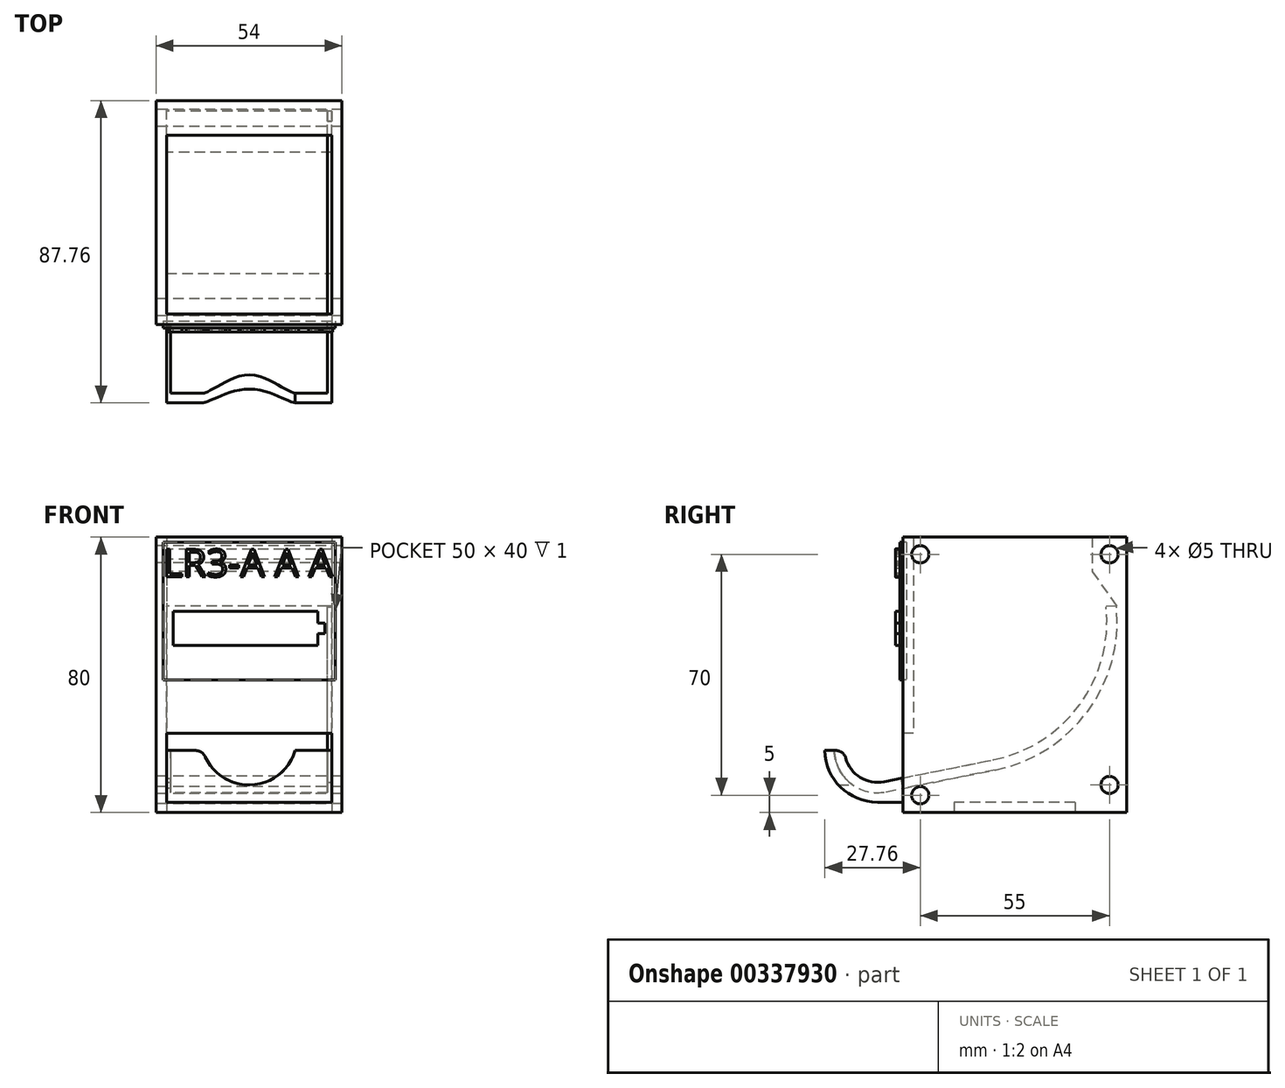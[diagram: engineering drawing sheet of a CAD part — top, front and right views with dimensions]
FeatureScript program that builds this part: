
annotation { "Feature Type Name" : "Feature", "Feature Type Description" : "" }
export const myFeature = defineFeature(function(context is Context, id is Id, definition is map)
    precondition{}
    {
        {
            var Q0;
            Q0=qCreatedBy(makeId("Top.planeOp"),FACE);
            var sketch = newSketch(context, id + "F0", { "sketchPlane" : qUnion([Q0])});
            skLineSegment(sketch, "E0", {"start": v(-27, 65) * mm, "end": v(-27, 0) * mm});
            skLineSegment(sketch, "E1", {"start": v(-27, 0) * mm, "end": v(27, 0) * mm});
            skLineSegment(sketch, "E2", {"start": v(27, 0) * mm, "end": v(27, 65) * mm});
            skLineSegment(sketch, "E3.0", {"start": v(-24, 65) * mm, "end": v(-24, 3) * mm});
            skLineSegment(sketch, "E4.0", {"start": v(-24, 3) * mm, "end": v(24, 3) * mm});
            skLineSegment(sketch, "E5.0", {"start": v(24, 3) * mm, "end": v(24, 65) * mm});
            skLineSegment(sketch, "E6", {"start": v(-27, 65) * mm, "end": v(-24, 65) * mm});
            skLineSegment(sketch, "E7", {"start": v(24, 65) * mm, "end": v(27, 65) * mm});
            skSolve(sketch);
        }
        {
            var Q0;
            Q0=qSketchRegion(id+"F0",true);
            extrude(context, id + "F1", {"entities" : qUnion([Q0]), "depth" : 80 * mm});
        }
        {
            var Q0;
            Q0=makeQuery(id+"F1.opExtrude","SWEPT_FACE",FACE,{"disambiguationData":[OSD([sQuery(id+"F0.wireOp",EDGE,"E1")])]});
            var sketch = newSketch(context, id + "F2", { "sketchPlane" : qUnion([Q0])});
            skLineSegment(sketch, "E8.bottom", {"start": v(-24, 3) * mm, "end": v(24, 3) * mm});
            skLineSegment(sketch, "E8.top", {"start": v(-24, 23) * mm, "end": v(24, 23) * mm});
            skLineSegment(sketch, "E8.left", {"start": v(-24, 3) * mm, "end": v(-24, 23) * mm});
            skLineSegment(sketch, "E8.right", {"start": v(24, 3) * mm, "end": v(24, 23) * mm});
            skSolve(sketch);
        }
        {
            var Q0;
            Q0=makeQuery(id+"F2.imprint","IMPRINT",FACE,{"disambiguationData":[TD([[makeQuery(id+"F2.imprint","IMPRINT",EDGE,{"derivedFrom":sQuery(id+"F2.wireOp",EDGE,"E8.bottom")}),1.0]])]});
            extrude(context, id + "F3", {"entities" : qUnion([Q0]), "operationType" : NewBodyOperationType.REMOVE, "endBound" : BoundingType.THROUGH_ALL, "oppositeDirection" : true, "depth" : 25 * mm});
        }
        {
            var Q0;
            {var subQ1=sQuery(id+"F0.wireOp",EDGE,"E4.0");Q0=makeQuery(id+"F3.boolean.opBoolean","SPLIT",FACE,{"disambiguationData":[TD([makeQuery(id+"F3.opExtrude","SWEPT_FACE",FACE,{"disambiguationData":[OSD([sQuery(id+"F2.wireOp",EDGE,"E8.bottom")])]})])],"derivedFrom":makeQuery(id+"F1.opExtrude","SWEPT_FACE",FACE,{"disambiguationData":[OSD([subQ1])]})});}
            extrude(context, id + "F4", {"entities" : qUnion([Q0]), "operationType" : NewBodyOperationType.ADD, "depth" : 11.8 * mm});
        }
        {
            var Q0;
            Q0=makeQuery(id+"F1.opExtrude","SWEPT_FACE",FACE,{"disambiguationData":[OSD([sQuery(id+"F0.wireOp",EDGE,"E1")])]});
            var sketch = newSketch(context, id + "F5", { "sketchPlane" : qUnion([Q0])});
            skLineSegment(sketch, "E9.bottom", {"start": v(-25, 78.5) * mm, "end": v(25, 78.5) * mm});
            skLineSegment(sketch, "E9.top", {"start": v(-25, 38.5) * mm, "end": v(25, 38.5) * mm});
            skLineSegment(sketch, "E9.left", {"start": v(-25, 78.5) * mm, "end": v(-25, 38.5) * mm});
            skLineSegment(sketch, "E9.right", {"start": v(25, 78.5) * mm, "end": v(25, 38.5) * mm});
            skSolve(sketch);
        }
        {
            var Q0;
            Q0=qSketchRegion(id+"F5",true);
            extrude(context, id + "F6", {"entities" : qUnion([Q0]), "operationType" : NewBodyOperationType.REMOVE, "oppositeDirection" : true, "depth" : 1 * mm});
        }
        {
            var Q0;
            Q0=qSketchRegion(id+"F5",true);
            extrude(context, id + "F7", {"entities" : qUnion([Q0]), "depth" : 1 * mm});
        }
        {
            var Q0;
            Q0=makeQuery(id+"F7.opExtrude","CAP_FACE",FACE,{"disambiguationData":[OSD([sQuery(id+"F5.wireOp",EDGE,"E9.bottom"),sQuery(id+"F5.wireOp",EDGE,"E9.top"),sQuery(id+"F5.wireOp",EDGE,"E9.left"),sQuery(id+"F5.wireOp",EDGE,"E9.right")])],"isStart":false});
            var sketch = newSketch(context, id + "F8", { "sketchPlane" : qUnion([Q0])});
            skText(sketch, "E10", { "text": "LR3-A A A", "fontName": "OpenSans-Regular.ttf"});
            const initialGuessF8  = {"E10": [-0.02508, 0.0685, 1, 0, 0.008]};
            skSetInitialGuess(sketch, initialGuessF8);
            skSolve(sketch);
        }
        {
            var Q0;
            Q0=makeQuery(id+"F8.imprint","IMPRINT",FACE,{"disambiguationData":[TD([[makeQuery(id+"F8.imprint","IMPRINT",EDGE,{"derivedFrom":sQuery(id+"F8.wireOp",EDGE,"E10.sketch_text.stroke-0")}),1.0]])]});
            var sketch = newSketch(context, id + "F9", { "sketchPlane" : qUnion([Q0])});
            skLineSegment(sketch, "E11.bottom", {"start": v(-22, 58.5) * mm, "end": v(20, 58.5) * mm});
            skLineSegment(sketch, "E11.top", {"start": v(-22, 48.5) * mm, "end": v(20, 48.5) * mm});
            skLineSegment(sketch, "E11.left", {"start": v(-22, 58.5) * mm, "end": v(-22, 48.5) * mm});
            skLineSegment(sketch, "E11.right", {"start": v(20, 58.5) * mm, "end": v(20, 55) * mm});
            skPoint(sketch, "E12.oppositeSnap0", {"position": v(20, 53.5) * mm});
            skLineSegment(sketch, "E12.bottom", {"start": v(20, 55) * mm, "end": v(22, 55) * mm});
            skLineSegment(sketch, "E13.trimOffspring", {"start": v(20, 52) * mm, "end": v(20, 48.5) * mm});
            skLineSegment(sketch, "E14", {"start": v(22, 55) * mm, "end": v(22, 52) * mm});
            skLineSegment(sketch, "E15", {"start": v(22, 52) * mm, "end": v(20, 52) * mm});
            skSolve(sketch);
        }
        {
            var Q0;
            Q0=makeQuery(id+"F9.imprint","IMPRINT",FACE,{"disambiguationData":[TD([[makeQuery(id+"F9.imprint","IMPRINT",EDGE,{"derivedFrom":sQuery(id+"F9.wireOp",EDGE,"E11.bottom")}),-1.0]])]});
            extrude(context, id + "F10", {"entities" : qUnion([Q0]), "operationType" : NewBodyOperationType.ADD, "depth" : 1.2 * mm});
        }
        {
            var Q0;
            Q0=qSketchRegion(id+"F8",true);
            extrude(context, id + "F11", {"entities" : qUnion([Q0]), "operationType" : NewBodyOperationType.ADD, "depth" : 1.2 * mm});
        }
        {
            var Q0;
            Q0=makeQuery(id+"F1.opExtrude","SWEPT_FACE",FACE,{"disambiguationData":[OSD([sQuery(id+"F0.wireOp",EDGE,"E7")])]});
            var sketch = newSketch(context, id + "F12", { "sketchPlane" : qUnion([Q0])});
            skLineSegment(sketch, "E16.bottom", {"start": v(-24, 3) * mm, "end": v(24, 3) * mm});
            skLineSegment(sketch, "E16.top", {"start": v(-24, 0) * mm, "end": v(24, 0) * mm});
            skLineSegment(sketch, "E16.left", {"start": v(-24, 3) * mm, "end": v(-24, 0) * mm});
            skLineSegment(sketch, "E16.right", {"start": v(24, 3) * mm, "end": v(24, 0) * mm});
            skSolve(sketch);
        }
        {
            var Q0;
            Q0=makeQuery(id+"F12.imprint","IMPRINT",FACE,{"disambiguationData":[TD([[makeQuery(id+"F12.imprint","IMPRINT",EDGE,{"derivedFrom":sQuery(id+"F12.wireOp",EDGE,"E16.bottom")}),-1.0]])]});
            extrude(context, id + "F13", {"entities" : qUnion([Q0]), "operationType" : NewBodyOperationType.ADD, "oppositeDirection" : true, "depth" : 15 * mm});
        }
        {
            var Q0;
            Q0=qCreatedBy(makeId("Right.planeOp"),FACE);
            var sketch = newSketch(context, id + "F14", { "sketchPlane" : qUnion([Q0])});
            skLineSegment(sketch, "E17", {"start": v(65, 80) * mm, "end": v(55, 80) * mm});
            skLineSegment(sketch, "E18", {"start": v(55, 80) * mm, "end": v(55, 70) * mm});
            skLineSegment(sketch, "E19", {"start": v(55, 70) * mm, "end": v(62, 60) * mm});
            skLineSegment(sketch, "E20", {"start": v(65, 80) * mm, "end": v(65, 3) * mm});
            skLineSegment(sketch, "E21", {"start": v(65, 3) * mm, "end": v(-7.46, 3) * mm});
            skArc(sketch, "E22", {"start": v(26.86, 12.37) * mm, "mid": v(53.63, 29.4) * mm, "end": v(62, 60) * mm});
            skLineSegment(sketch, "E23", {"start": v(-22.76, 18) * mm, "end": v(-20, 18) * mm});
            skLineSegment(sketch, "E24", {"start": v(26.86, 12.37) * mm, "end": v(-5, 6) * mm});
            skArc(sketch, "E25", {"start": v(-5, 6) * mm, "mid": v(-15.3, 8.5) * mm, "end": v(-20, 18) * mm});
            skArc(sketch, "E26", {"start": v(-7.46, 3) * mm, "mid": v(-18.17, 7.38) * mm, "end": v(-22.76, 18) * mm});
            skPoint(sketch, "E27", {"position": v(0, 7) * mm});
            skSolve(sketch);
        }
        {
            var Q0;
            Q0=makeQuery(id+"F14.imprint","IMPRINT",FACE,{"disambiguationData":[TD([[makeQuery(id+"F14.imprint","IMPRINT",EDGE,{"derivedFrom":sQuery(id+"F14.wireOp",EDGE,"E17")}),1.0]])]});
            extrude(context, id + "F15", {"entities" : qUnion([Q0]), "endBound" : BoundingType.SYMMETRIC, "depth" : 48 * mm});
        }
        {
            var Q0;
            Q0=qCreatedBy(makeId("Right.planeOp"),FACE);
            var sketch = newSketch(context, id + "F16", { "sketchPlane" : qUnion([Q0])});
            skCircle(sketch, "E28", {"center": v(60, 75) * mm, "radius": 2.5 * mm});
            skCircle(sketch, "E29", {"center": v(60, 8) * mm, "radius": 2.5 * mm});
            skCircle(sketch, "E30", {"center": v(5, 75) * mm, "radius": 2.5 * mm});
            skCircle(sketch, "E31", {"center": v(5, 5) * mm, "radius": 2.5 * mm});
            skSolve(sketch);
        }
        {
            var Q0;
            Q0=qSketchRegion(id+"F16",true);
            extrude(context, id + "F17", {"entities" : qUnion([Q0]), "operationType" : NewBodyOperationType.REMOVE, "endBound" : BoundingType.SYMMETRIC, "depth" : 60 * mm});
        }
        {
            var Q0;
            Q0=makeQuery(id+"F15.opExtrude","SWEPT_FACE",FACE,{"disambiguationData":[OSD([sQuery(id+"F14.wireOp",EDGE,"E23")])]});
            var sketch = newSketch(context, id + "F18", { "sketchPlane" : qUnion([Q0])});
            skLineSegment(sketch, "E32.bottom", {"start": v(22.8, -20) * mm, "end": v(24, -20) * mm});
            skLineSegment(sketch, "E32.top", {"start": v(22.8, -17) * mm, "end": v(24, -17) * mm});
            skLineSegment(sketch, "E32.left", {"start": v(22.8, -20) * mm, "end": v(22.8, -17) * mm});
            skLineSegment(sketch, "E32.right", {"start": v(24, -20) * mm, "end": v(24, -17) * mm});
            skLineSegment(sketch, "E33.bottom", {"start": v(-24, -20) * mm, "end": v(-22.8, -20) * mm});
            skLineSegment(sketch, "E33.top", {"start": v(-24, -17) * mm, "end": v(-22.8, -17) * mm});
            skLineSegment(sketch, "E33.left", {"start": v(-24, -20) * mm, "end": v(-24, -17) * mm});
            skLineSegment(sketch, "E33.right", {"start": v(-22.8, -20) * mm, "end": v(-22.8, -17) * mm});
            skSolve(sketch);
        }
        {
            var Q0;
            Q0=makeQuery(id+"F18.imprint","IMPRINT",FACE,{"disambiguationData":[TD([[makeQuery(id+"F18.imprint","IMPRINT",EDGE,{"derivedFrom":sQuery(id+"F18.wireOp",EDGE,"E32.bottom")}),-1.0]])]});
            var Q1;
            Q1=makeQuery(id+"F15.opExtrude","CAP_EDGE",EDGE,{"disambiguationData":[OSD([sQuery(id+"F14.wireOp",EDGE,"E25")])],"isStart":false});
            var Q2;
            Q2=makeQuery(id+"F15.opExtrude","CAP_EDGE",EDGE,{"disambiguationData":[OSD([sQuery(id+"F14.wireOp",EDGE,"E24")])],"isStart":false});
            var Q3;
            Q3=makeQuery(id+"F15.opExtrude","CAP_EDGE",EDGE,{"disambiguationData":[OSD([sQuery(id+"F14.wireOp",EDGE,"E22")])],"isStart":false});
            sweep(context, id + "F19", {"operationType" : NewBodyOperationType.ADD, "profiles" : qUnion([Q0]), "path" : qUnion([Q1, Q2, Q3])});
        }
        {
            var Q0;
            Q0=makeQuery(id+"F18.imprint","IMPRINT",FACE,{"disambiguationData":[TD([[makeQuery(id+"F18.imprint","IMPRINT",EDGE,{"derivedFrom":sQuery(id+"F18.wireOp",EDGE,"E33.bottom")}),-1.0]])]});
            var Q1;
            Q1=makeQuery(id+"F15.opExtrude","CAP_EDGE",EDGE,{"disambiguationData":[OSD([sQuery(id+"F14.wireOp",EDGE,"E25")])],"isStart":true});
            var Q2;
            Q2=makeQuery(id+"F15.opExtrude","CAP_EDGE",EDGE,{"disambiguationData":[OSD([sQuery(id+"F14.wireOp",EDGE,"E24")])],"isStart":true});
            var Q3;
            Q3=makeQuery(id+"F15.opExtrude","CAP_EDGE",EDGE,{"disambiguationData":[OSD([sQuery(id+"F14.wireOp",EDGE,"E22")])],"isStart":true});
            sweep(context, id + "F20", {"operationType" : NewBodyOperationType.ADD, "profiles" : qUnion([Q0]), "path" : qUnion([Q1, Q2, Q3])});
        }
        {
            var Q0;
            Q0=qCreatedBy(makeId("Front.planeOp"),FACE);
            var sketch = newSketch(context, id + "F21", { "sketchPlane" : qUnion([Q0])});
            skArc(sketch, "E34", {"start": v(-13.42, 18) * mm, "mid": v(0, 8) * mm, "end": v(13.42, 18) * mm});
            skLineSegment(sketch, "E35", {"start": v(-13.42, 18) * mm, "end": v(13.42, 18) * mm});
            skSolve(sketch);
        }
        {
            var Q0;
            Q0=makeQuery(id+"F21.imprint","IMPRINT",FACE,{"disambiguationData":[TD([[makeQuery(id+"F21.imprint","IMPRINT",EDGE,{"derivedFrom":sQuery(id+"F21.wireOp",EDGE,"E34")}),1.0]])]});
            extrude(context, id + "F22", {"entities" : qUnion([Q0]), "operationType" : NewBodyOperationType.REMOVE, "endBound" : BoundingType.THROUGH_ALL, "depth" : 25 * mm});
        }
        {
            var Q0;
            {var subQ0=sQuery(id+"F21.wireOp",EDGE,"E35");var subQ1=sQuery(id+"F21.wireOp",EDGE,"E34");Q0=makeQuery(id+"F22.boolean.opBoolean","COPY",EDGE,{"derivedFrom":makeQuery(id+"F22.opExtrude","SWEPT_EDGE",EDGE,{"disambiguationData":[OSD([subQ1,subQ0]),TDD([makeQuery(id+"F21.imprint","INTERSECT",VERTEX,{"disambiguationData":[OD(1.0)],"derivedFrom":[subQ1,subQ0]})])]})});}
            var Q1;
            {var subQ0=sQuery(id+"F21.wireOp",EDGE,"E35");var subQ1=sQuery(id+"F21.wireOp",EDGE,"E34");Q1=makeQuery(id+"F22.boolean.opBoolean","COPY",EDGE,{"derivedFrom":makeQuery(id+"F22.opExtrude","SWEPT_EDGE",EDGE,{"disambiguationData":[OSD([subQ1,subQ0]),TDD([makeQuery(id+"F21.imprint","INTERSECT",VERTEX,{"disambiguationData":[OD(0.0)],"derivedFrom":[subQ1,subQ0]})])]})});}
            fillet(context, id + "F23", {"entities" : qUnion([Q0, Q1]), "radius" : 3.1 * mm, "tangentPropagation" : true, "allowEdgeOverflow" : false});
        }
        {
            var Q0;
            Q0=makeQuery(id+"F20.opSweep","CAP_EDGE",EDGE,{"disambiguationData":[OSD([sQuery(id+"F14.wireOp",EDGE,"E23"),sQuery(id+"F14.wireOp",EDGE,"E25"),sQuery(id+"F18.wireOp",EDGE,"E33.top")])],"isStart":true});
            var Q1;
            Q1=makeQuery(id+"F19.opSweep","CAP_EDGE",EDGE,{"disambiguationData":[OSD([sQuery(id+"F14.wireOp",EDGE,"E23"),sQuery(id+"F14.wireOp",EDGE,"E25"),sQuery(id+"F18.wireOp",EDGE,"E32.top")])],"isStart":true});
            fillet(context, id + "F24", {"entities" : qUnion([Q0, Q1]), "radius" : 3 * mm, "tangentPropagation" : true, "allowEdgeOverflow" : false});
        }
    });
